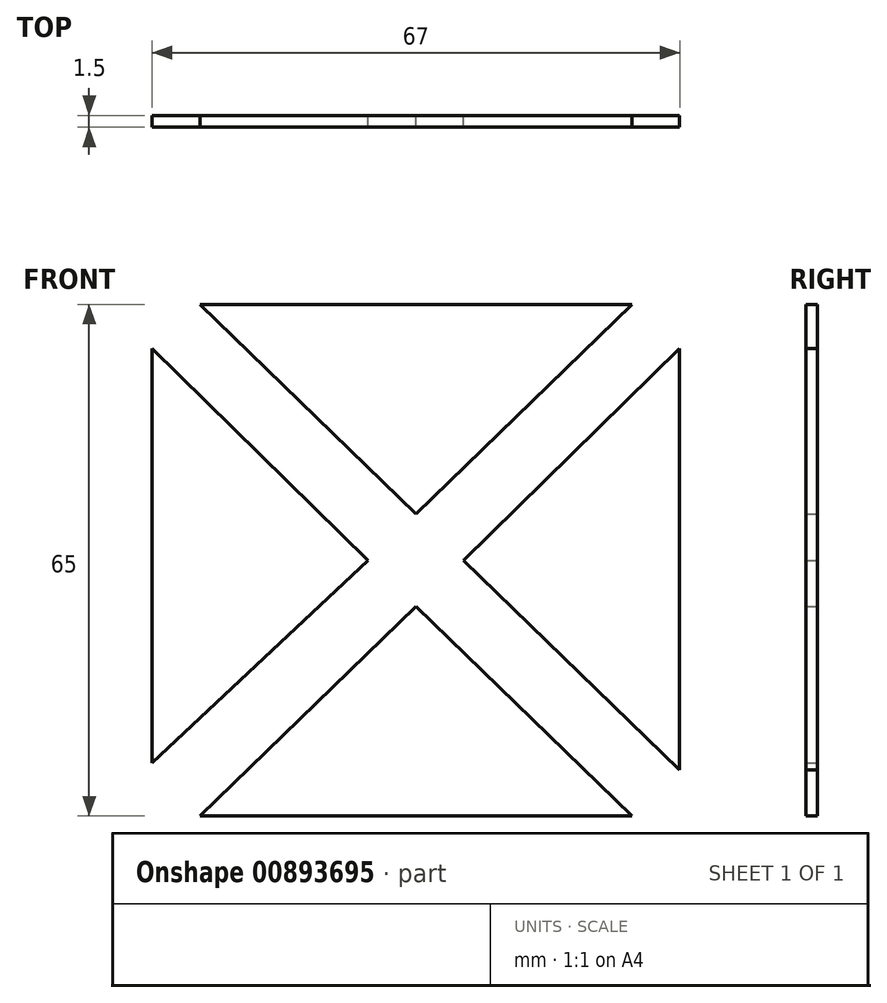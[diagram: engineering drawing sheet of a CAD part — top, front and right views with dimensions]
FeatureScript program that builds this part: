
annotation { "Feature Type Name" : "Feature", "Feature Type Description" : "" }
export const myFeature = defineFeature(function(context is Context, id is Id, definition is map)
    precondition{}
    {
        {
            var Q0;
            Q0=qCreatedBy(makeId("Front.planeOp"),FACE);
            var sketch = newSketch(context, id + "F0", { "sketchPlane" : qUnion([Q0])});
            skLineSegment(sketch, "E0.bottom", {"start": v(-71.62, -13.02) * mm, "end": v(-4.62, -13.02) * mm});
            skLineSegment(sketch, "E0.top", {"start": v(-71.62, -78.02) * mm, "end": v(-4.62, -78.02) * mm});
            skLineSegment(sketch, "E0.left", {"start": v(-71.62, -13.02) * mm, "end": v(-71.62, -78.02) * mm});
            skLineSegment(sketch, "E0.right", {"start": v(-4.62, -13.02) * mm, "end": v(-4.62, -78.02) * mm});
            skLineSegment(sketch, "E1", {"start": v(-71.62, -71.24) * mm, "end": v(-44.19, -45.52) * mm});
            skLineSegment(sketch, "E2", {"start": v(-44.19, -45.52) * mm, "end": v(-71.62, -18.62) * mm});
            skLineSegment(sketch, "E3", {"start": v(-65.56, -13.02) * mm, "end": v(-38.12, -39.64) * mm});
            skLineSegment(sketch, "E4", {"start": v(-38.12, -39.64) * mm, "end": v(-10.69, -13.02) * mm});
            skLineSegment(sketch, "E5", {"start": v(-32.06, -45.52) * mm, "end": v(-4.62, -18.62) * mm});
            skLineSegment(sketch, "E6", {"start": v(-32.06, -45.52) * mm, "end": v(-4.62, -72.14) * mm});
            skLineSegment(sketch, "E7", {"start": v(-10.5, -78.2) * mm, "end": v(-38.12, -51.4) * mm});
            skLineSegment(sketch, "E8", {"start": v(-38.12, -51.4) * mm, "end": v(-65.75, -78.2) * mm});
            skSolve(sketch);
        }
        {
            var Q0;
            {var subQ0=sQuery(id+"F0.wireOp",EDGE,"u1IieLPx-6mnN-yTEg-K28m-5tTml9aKwXlB");Q0=makeQuery(id+"F0.imprint","IMPRINT",FACE,{"disambiguationData":[TD([[makeQuery(id+"F0.imprint","IMPRINT",EDGE,{"derivedFrom":subQ0}),-1.0]])]});}
            var Q1;
            {var subQ0=sQuery(id+"F0.wireOp",EDGE,"PaWdvUsL-E5RP-xxMY-DYju-ZVmQGgb5IrXT");Q1=makeQuery(id+"F0.imprint","IMPRINT",FACE,{"disambiguationData":[TD([[makeQuery(id+"F0.imprint","IMPRINT",EDGE,{"derivedFrom":subQ0}),1.0]])]});}
            var Q2;
            {var subQ0=sQuery(id+"F0.wireOp",EDGE,"jJIlaCJ4-q6Ju-z6HG-haay-sYPvqm6y6kxW");Q2=makeQuery(id+"F0.imprint","IMPRINT",FACE,{"disambiguationData":[TD([[makeQuery(id+"F0.imprint","IMPRINT",EDGE,{"derivedFrom":subQ0}),1.0]])]});}
            var Q3;
            {var subQ0=sQuery(id+"F0.wireOp",EDGE,"atbIKI4T-SNVk-Rk2K-SPi8-B6mGmF8wrnq0");Q3=makeQuery(id+"F0.imprint","IMPRINT",FACE,{"disambiguationData":[TD([[makeQuery(id+"F0.imprint","IMPRINT",EDGE,{"derivedFrom":subQ0}),1.0]])]});}
            var Q4;
            {var subQ0=sQuery(id+"F0.wireOp",EDGE,"E3");Q4=makeQuery(id+"F0.imprint","IMPRINT",FACE,{"disambiguationData":[TD([[makeQuery(id+"F0.imprint","IMPRINT",EDGE,{"derivedFrom":subQ0}),1.0]])]});}
            var Q5;
            {var subQ0=sQuery(id+"F0.wireOp",EDGE,"E8");var subQ1=sQuery(id+"F0.wireOp",EDGE,"E0.top");var subQ2=makeQuery(id+"F0.imprint","INTERSECT",VERTEX,{"derivedFrom":[subQ1,subQ0]});Q5=makeQuery(id+"F0.imprint","IMPRINT",FACE,{"disambiguationData":[TD([[makeQuery(id+"F0.imprint","IMPRINT",EDGE,{"disambiguationData":[TD([[subQ2,-1.0]])],"derivedFrom":subQ1}),1.0]])]});}
            var Q6;
            {var subQ0=sQuery(id+"F0.wireOp",EDGE,"E5");Q6=makeQuery(id+"F0.imprint","IMPRINT",FACE,{"disambiguationData":[TD([[makeQuery(id+"F0.imprint","IMPRINT",EDGE,{"derivedFrom":subQ0}),-1.0]])]});}
            var Q7;
            {var subQ0=sQuery(id+"F0.wireOp",EDGE,"E1");Q7=makeQuery(id+"F0.imprint","IMPRINT",FACE,{"disambiguationData":[TD([[makeQuery(id+"F0.imprint","IMPRINT",EDGE,{"derivedFrom":subQ0}),1.0]])]});}
            extrude(context, id + "F1", {"entities" : qUnion([Q0, Q1, Q2, Q3, Q4, Q5, Q6, Q7]), "depth" : 1.5 * mm, "offsetDistance" : 25 * mm});
        }
        {
            var Q0;
            Q0=qCreatedBy(makeId("Front.planeOp"),FACE);
            cPlane(context, id + "F2", {"entities" : qUnion([Q0]), "cplaneType" : CPlaneType.OFFSET, "offset" : 1.5 * mm, "width" : 150 * mm, "height" : 150 * mm});
        }
    });
